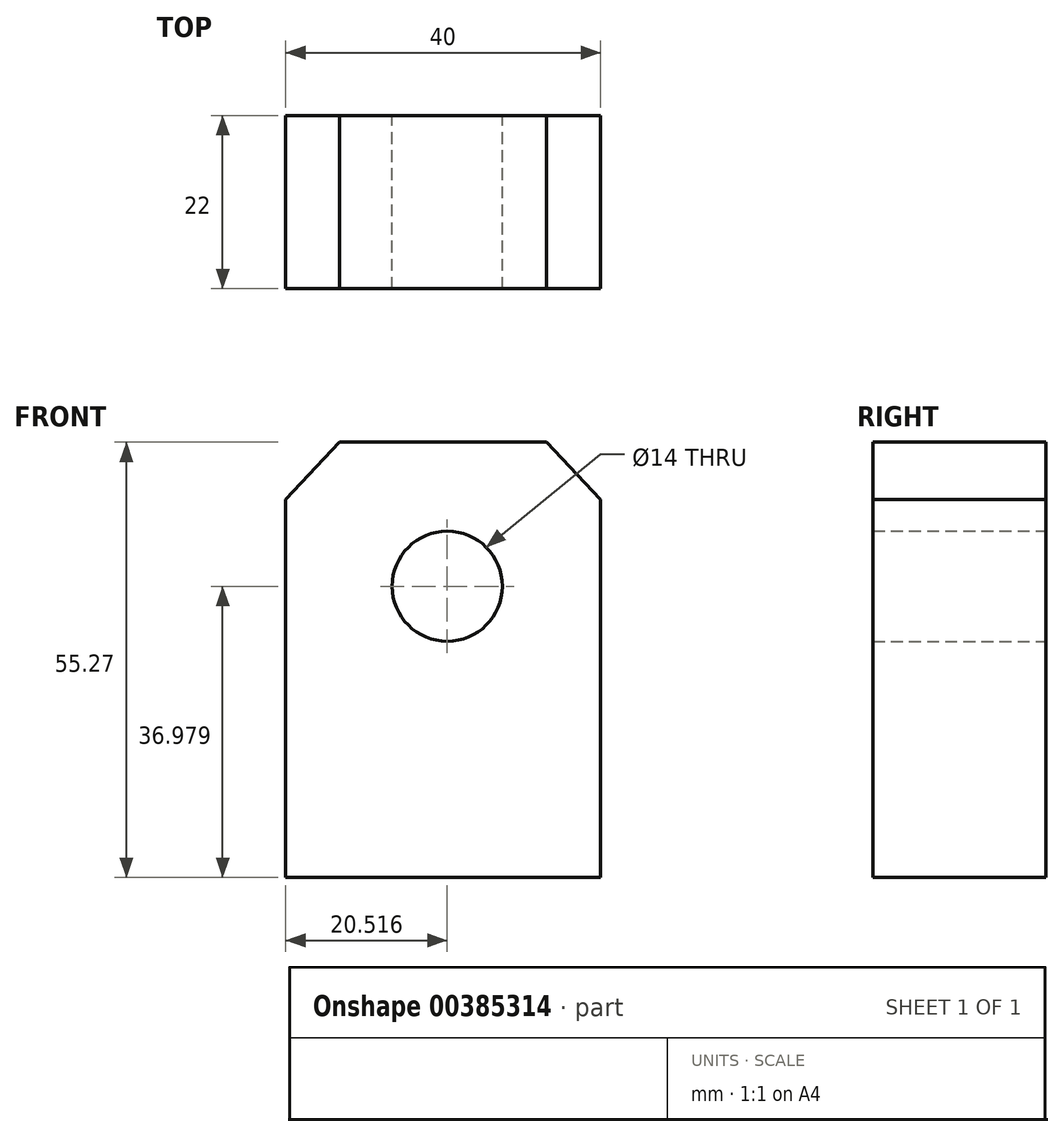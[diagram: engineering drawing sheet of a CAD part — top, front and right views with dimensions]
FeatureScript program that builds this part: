
annotation { "Feature Type Name" : "Feature", "Feature Type Description" : "" }
export const myFeature = defineFeature(function(context is Context, id is Id, definition is map)
    precondition{}
    {
        {
            var Q0;
            Q0=qCreatedBy(makeId("Front.planeOp"),FACE);
            var sketch = newSketch(context, id + "F0", { "sketchPlane" : qUnion([Q0])});
            skLineSegment(sketch, "E0", {"start": v(0, 0) * mm, "end": v(0, -47.98) * mm});
            skLineSegment(sketch, "E1", {"start": v(0, -47.98) * mm, "end": v(40, -47.98) * mm});
            skLineSegment(sketch, "E2", {"start": v(40, -47.98) * mm, "end": v(40, 0) * mm});
            skCircle(sketch, "E3", {"center": v(20.52, -11) * mm, "radius": 7 * mm});
            skLineSegment(sketch, "E4", {"start": v(0, 0) * mm, "end": v(6.85, 7.3) * mm});
            skLineSegment(sketch, "E5", {"start": v(40, 0) * mm, "end": v(33.15, 7.3) * mm});
            skLineSegment(sketch, "E6", {"start": v(33.15, 7.3) * mm, "end": v(6.85, 7.3) * mm});
            skSolve(sketch);
        }
        {
            var Q0;
            Q0 = qSketchRegion(id + "F0", true);
            extrude(context, id + "F1", {"entities" : qUnion([Q0]), "depth" : 22 * mm});
        }
    });
